FCSTD DOCUMENT  (FreeCAD 0.19R24276 (Git))
Label: MS_1
License: All rights reserved
LicenseURL: http://en.wikipedia.org/wiki/All_rights_reserved
objects: Sketcher::SketchObject×1, PartDesign::Body×1
note: 2 computed .brp shape members not serialized (recipe doc carries the construction recipe); baked Part::Feature solids carry a one-line shape summary decoded from their .brp

FEATURE [Sketcher::SketchObject] Sketch
  FullyConstrained = false
  MapMode = 5
  Support = -> [XY_Plane]
  sketch-geometry (3):
    g0: Circle CenterX=0 CenterY=0 CenterZ=0 NormalX=0 NormalY=0 NormalZ=1 AngleXU=0 Radius=62
    g1: Circle CenterX=46 CenterY=0 CenterZ=0 NormalX=0 NormalY=0 NormalZ=1 AngleXU=0 Radius=16
    g2: Circle CenterX=-46 CenterY=0 CenterZ=0 NormalX=0 NormalY=0 NormalZ=1 AngleXU=0 Radius=16
  constraints (7):
    c: Coincident(g0,g-1)
    c: DistanceX(g0,g1) = 46
    c: Diameter(g0) = 124
    c: Diameter(g1) = 32
    c: PointOnObject(g2,g-1)
    c: Equal(g2,g1)
    c: DistanceX(g2,g0) = 46
FEATURE [PartDesign::Body] Body
  Group = -> [Sketch]
  Origin = -> Origin
